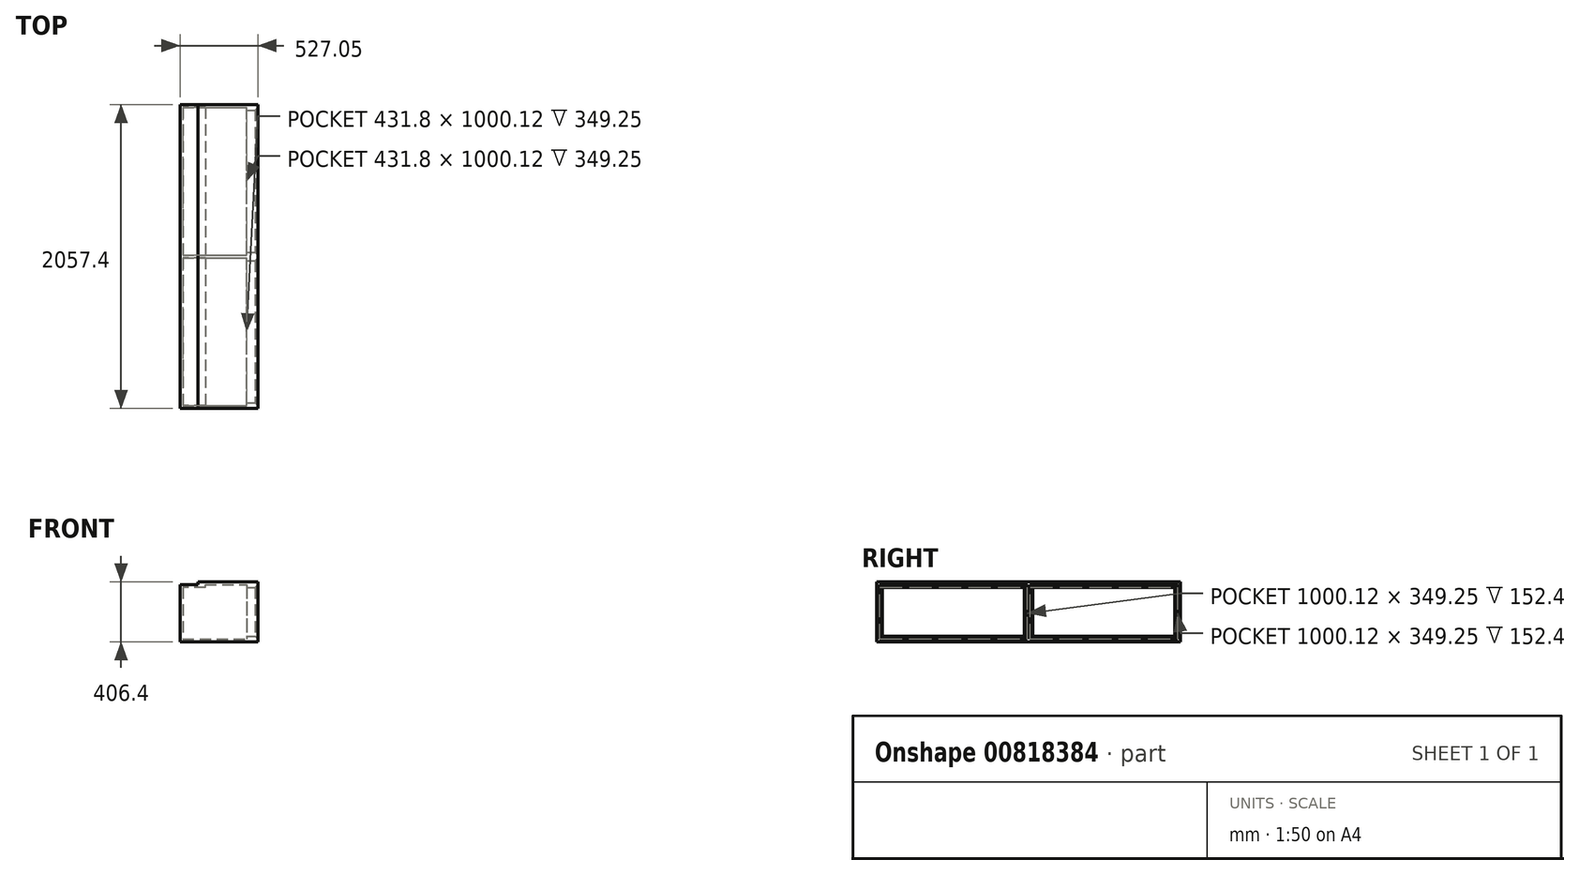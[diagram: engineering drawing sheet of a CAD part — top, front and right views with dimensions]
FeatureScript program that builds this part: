
annotation { "Feature Type Name" : "Feature", "Feature Type Description" : "" }
export const myFeature = defineFeature(function(context is Context, id is Id, definition is map)
    precondition{}
    {
        {
            var Q0;
            Q0=qCreatedBy(makeId("Right.planeOp"),FACE);
            var sketch = newSketch(context, id + "F0", { "sketchPlane" : qUnion([Q0])});
            skLineSegment(sketch, "E0.bottom", {"start": v(-1028.7, 203.2) * mm, "end": v(1028.7, 203.2) * mm});
            skLineSegment(sketch, "E0.top", {"start": v(-1028.7, -203.2) * mm, "end": v(1028.7, -203.2) * mm});
            skLineSegment(sketch, "E0.left", {"start": v(-1028.7, 203.2) * mm, "end": v(-1028.7, -203.2) * mm});
            skLineSegment(sketch, "E0.right", {"start": v(1028.7, 203.2) * mm, "end": v(1028.7, -203.2) * mm});
            skLineSegment(sketch, "E1", {"start": v(-1028.7, 203.2) * mm, "end": v(1028.7, -203.2) * mm, "construction": true});
            skLineSegment(sketch, "E2.0", {"start": v(-1009.65, 184.15) * mm, "end": v(-9.53, 184.15) * mm});
            skLineSegment(sketch, "E2.1", {"start": v(-1009.65, 184.15) * mm, "end": v(-1009.65, -184.15) * mm});
            skLineSegment(sketch, "E2.2", {"start": v(-1009.65, -184.15) * mm, "end": v(-9.53, -184.15) * mm});
            skLineSegment(sketch, "E2.3", {"start": v(1009.65, 184.15) * mm, "end": v(1009.65, -184.15) * mm});
            skLineSegment(sketch, "E3", {"start": v(0, 184.15) * mm, "end": v(0, -184.15) * mm, "construction": true});
            skLineSegment(sketch, "E4.0", {"start": v(-9.52, 184.15) * mm, "end": v(-9.53, -184.15) * mm});
            skLineSegment(sketch, "E5.MirrorCS", {"start": v(9.52, 184.15) * mm, "end": v(9.53, -184.15) * mm});
            skLineSegment(sketch, "E6.trimOffspring", {"start": v(9.53, 184.15) * mm, "end": v(1009.65, 184.15) * mm});
            skLineSegment(sketch, "E7.trimOffspring", {"start": v(9.53, -184.15) * mm, "end": v(1009.65, -184.15) * mm});
            skSolve(sketch);
        }
        {
            var Q0;
            Q0=makeQuery(id+"F0.imprint","IMPRINT",FACE,{"disambiguationData":[TD([[makeQuery(id+"F0.imprint","IMPRINT",EDGE,{"derivedFrom":sQuery(id+"F0.wireOp",EDGE,"E0.bottom")}),-1.0]])]});
            extrude(context, id + "F1", {"entities" : qUnion([Q0]), "oppositeDirection" : true, "depth" : 508 * mm, "offsetDistance" : 25.4 * mm});
        }
        {
            var Q0;
            Q0=makeQuery(id+"F1.opExtrude","SWEPT_FACE",FACE,{"disambiguationData":[OSD([sQuery(id+"F0.wireOp",EDGE,"E0.left")])]});
            var sketch = newSketch(context, id + "F2", { "sketchPlane" : qUnion([Q0])});
            skLineSegment(sketch, "E8.bottom", {"start": v(-508, 203.2) * mm, "end": v(-406.4, 203.2) * mm});
            skLineSegment(sketch, "E8.top", {"start": v(-508, 184.15) * mm, "end": v(-406.4, 184.15) * mm});
            skLineSegment(sketch, "E8.left", {"start": v(-508, 203.2) * mm, "end": v(-508, 184.15) * mm});
            skLineSegment(sketch, "E8.right", {"start": v(-406.4, 203.2) * mm, "end": v(-406.4, 184.15) * mm});
            skSolve(sketch);
        }
        {
            var Q0;
            Q0 = qSketchRegion(id + "F2", true);
            extrude(context, id + "F3", {"entities" : qUnion([Q0]), "operationType" : NewBodyOperationType.REMOVE, "endBound" : BoundingType.THROUGH_ALL, "oppositeDirection" : true, "depth" : 25.4 * mm, "offsetDistance" : 25.4 * mm});
        }
        {
            var Q0;
            Q0=makeQuery(id+"F1.opExtrude","CAP_FACE",FACE,{"disambiguationData":[OSD([sQuery(id+"F0.wireOp",EDGE,"E0.bottom"),sQuery(id+"F0.wireOp",EDGE,"E0.top"),sQuery(id+"F0.wireOp",EDGE,"E0.left"),sQuery(id+"F0.wireOp",EDGE,"E0.right"),sQuery(id+"F0.wireOp",EDGE,"E2.0"),sQuery(id+"F0.wireOp",EDGE,"E2.1"),sQuery(id+"F0.wireOp",EDGE,"E2.2"),sQuery(id+"F0.wireOp",EDGE,"E2.3"),sQuery(id+"F0.wireOp",EDGE,"E4.0"),sQuery(id+"F0.wireOp",EDGE,"E5.MirrorCS"),sQuery(id+"F0.wireOp",EDGE,"E6.trimOffspring"),sQuery(id+"F0.wireOp",EDGE,"E7.trimOffspring")])],"isStart":false});
            var sketch = newSketch(context, id + "F4", { "sketchPlane" : qUnion([Q0])});
            skLineSegment(sketch, "E9.bottom", {"start": v(-1028.7, 184.15) * mm, "end": v(1028.7, 184.15) * mm});
            skLineSegment(sketch, "E9.top", {"start": v(-1028.7, -203.2) * mm, "end": v(1028.7, -203.2) * mm});
            skLineSegment(sketch, "E9.left", {"start": v(-1028.7, 184.15) * mm, "end": v(-1028.7, -203.2) * mm});
            skLineSegment(sketch, "E9.right", {"start": v(1028.7, 184.15) * mm, "end": v(1028.7, -203.2) * mm});
            skSolve(sketch);
        }
        {
            var Q0;
            Q0 = qSketchRegion(id + "F4", true);
            extrude(context, id + "F5", {"entities" : qUnion([Q0]), "operationType" : NewBodyOperationType.ADD, "depth" : 19.05 * mm, "offsetDistance" : 25.4 * mm});
        }
        {
            var Q0;
            Q0=makeQuery(id+"F1.opExtrude","SWEPT_FACE",FACE,{"disambiguationData":[OSD([sQuery(id+"F0.wireOp",EDGE,"E6.trimOffspring")])]});
            var sketch = newSketch(context, id + "F6", { "sketchPlane" : qUnion([Q0])});
            skLineSegment(sketch, "E10.bottom", {"start": v(-355.6, -1009.65) * mm, "end": v(-508, -1009.65) * mm});
            skLineSegment(sketch, "E10.top", {"start": v(-355.6, 0) * mm, "end": v(-508, 0) * mm});
            skLineSegment(sketch, "E10.left", {"start": v(-355.6, -1009.65) * mm, "end": v(-355.6, 0) * mm});
            skLineSegment(sketch, "E10.right", {"start": v(-508, -1009.65) * mm, "end": v(-508, 0) * mm});
            skLineSegment(sketch, "E11.bottom", {"start": v(-355.6, 9.52) * mm, "end": v(-508, 9.52) * mm});
            skLineSegment(sketch, "E11.top", {"start": v(-355.6, 1009.65) * mm, "end": v(-508, 1009.65) * mm});
            skLineSegment(sketch, "E11.left", {"start": v(-355.6, 9.52) * mm, "end": v(-355.6, 1009.65) * mm});
            skLineSegment(sketch, "E11.right", {"start": v(-508, 9.52) * mm, "end": v(-508, 1009.65) * mm});
            skSolve(sketch);
        }
        {
            var Q0;
            Q0 = qSketchRegion(id + "F6", true);
            extrude(context, id + "F7", {"entities" : qUnion([Q0]), "operationType" : NewBodyOperationType.ADD, "depth" : 19.05 * mm, "offsetDistance" : 25.4 * mm});
        }
        {
            var Q0;
            Q0=makeQuery(id+"F1.opExtrude","CAP_FACE",FACE,{"disambiguationData":[OSD([sQuery(id+"F0.wireOp",EDGE,"E0.bottom"),sQuery(id+"F0.wireOp",EDGE,"E0.top"),sQuery(id+"F0.wireOp",EDGE,"E0.left"),sQuery(id+"F0.wireOp",EDGE,"E0.right"),sQuery(id+"F0.wireOp",EDGE,"E2.0"),sQuery(id+"F0.wireOp",EDGE,"E2.1"),sQuery(id+"F0.wireOp",EDGE,"E2.2"),sQuery(id+"F0.wireOp",EDGE,"E2.3"),sQuery(id+"F0.wireOp",EDGE,"E4.0"),sQuery(id+"F0.wireOp",EDGE,"E5.MirrorCS"),sQuery(id+"F0.wireOp",EDGE,"E6.trimOffspring"),sQuery(id+"F0.wireOp",EDGE,"E7.trimOffspring")])],"isStart":true});
            var sketch = newSketch(context, id + "F8", { "sketchPlane" : qUnion([Q0])});
            skLineSegment(sketch, "E12.bottom", {"start": v(-1009.65, 184.15) * mm, "end": v(-9.53, 184.15) * mm});
            skLineSegment(sketch, "E12.top", {"start": v(-1009.65, -184.15) * mm, "end": v(-9.53, -184.15) * mm});
            skLineSegment(sketch, "E12.left", {"start": v(-1009.65, 184.15) * mm, "end": v(-1009.65, -184.15) * mm});
            skLineSegment(sketch, "E12.right", {"start": v(-9.53, 184.15) * mm, "end": v(-9.53, -184.15) * mm});
            skLineSegment(sketch, "E13.bottom", {"start": v(9.53, 184.15) * mm, "end": v(1009.65, 184.15) * mm});
            skLineSegment(sketch, "E13.top", {"start": v(9.53, -184.15) * mm, "end": v(1009.65, -184.15) * mm});
            skLineSegment(sketch, "E13.left", {"start": v(9.53, 184.15) * mm, "end": v(9.53, -184.15) * mm});
            skLineSegment(sketch, "E13.right", {"start": v(1009.65, 184.15) * mm, "end": v(1009.65, -184.15) * mm});
            skLineSegment(sketch, "E14.bottom", {"start": v(-990.6, 165.1) * mm, "end": v(-28.58, 165.1) * mm});
            skLineSegment(sketch, "E14.top", {"start": v(-990.6, -165.1) * mm, "end": v(-28.58, -165.1) * mm});
            skLineSegment(sketch, "E14.left", {"start": v(-990.6, 165.1) * mm, "end": v(-990.6, -165.1) * mm});
            skLineSegment(sketch, "E14.right", {"start": v(-28.58, 165.1) * mm, "end": v(-28.58, -165.1) * mm});
            skLineSegment(sketch, "E15.bottom", {"start": v(28.58, 165.1) * mm, "end": v(990.6, 165.1) * mm});
            skLineSegment(sketch, "E15.top", {"start": v(28.58, -165.1) * mm, "end": v(990.6, -165.1) * mm});
            skLineSegment(sketch, "E15.left", {"start": v(28.58, 165.1) * mm, "end": v(28.58, -165.1) * mm});
            skLineSegment(sketch, "E15.right", {"start": v(990.6, 165.1) * mm, "end": v(990.6, -165.1) * mm});
            skSolve(sketch);
        }
        {
            var Q0;
            Q0 = qSketchRegion(id + "F8", true);
            extrude(context, id + "F9", {"entities" : qUnion([Q0]), "operationType" : NewBodyOperationType.ADD, "oppositeDirection" : true, "depth" : 76.2 * mm, "offsetDistance" : 25.4 * mm});
        }
        {
            var Q0;
            Q0=makeQuery(id+"F9.opExtrude","CAP_EDGE",EDGE,{"disambiguationData":[OSD([sQuery(id+"F8.wireOp",EDGE,"E14.bottom")])],"isStart":true});
            var Q1;
            Q1=makeQuery(id+"F9.opExtrude","CAP_EDGE",EDGE,{"disambiguationData":[OSD([sQuery(id+"F8.wireOp",EDGE,"E14.left")])],"isStart":true});
            var Q2;
            Q2=makeQuery(id+"F9.opExtrude","CAP_EDGE",EDGE,{"disambiguationData":[OSD([sQuery(id+"F8.wireOp",EDGE,"E14.top")])],"isStart":true});
            var Q3;
            Q3=makeQuery(id+"F9.opExtrude","CAP_EDGE",EDGE,{"disambiguationData":[OSD([sQuery(id+"F8.wireOp",EDGE,"E14.right")])],"isStart":true});
            var Q4;
            Q4=makeQuery(id+"F9.opExtrude","CAP_EDGE",EDGE,{"disambiguationData":[OSD([sQuery(id+"F8.wireOp",EDGE,"E15.top")])],"isStart":true});
            var Q5;
            Q5=makeQuery(id+"F9.opExtrude","CAP_EDGE",EDGE,{"disambiguationData":[OSD([sQuery(id+"F8.wireOp",EDGE,"E15.left")])],"isStart":true});
            var Q6;
            Q6=makeQuery(id+"F9.opExtrude","CAP_EDGE",EDGE,{"disambiguationData":[OSD([sQuery(id+"F8.wireOp",EDGE,"E15.bottom")])],"isStart":true});
            var Q7;
            Q7=makeQuery(id+"F9.opExtrude","CAP_EDGE",EDGE,{"disambiguationData":[OSD([sQuery(id+"F8.wireOp",EDGE,"E15.right")])],"isStart":true});
            chamfer(context, id + "F10", {"entities" : qUnion([Q0, Q1, Q2, Q3, Q4, Q5, Q6, Q7]), "width" : 19.05 * mm, "tangentPropagation" : true});
        }
    });
